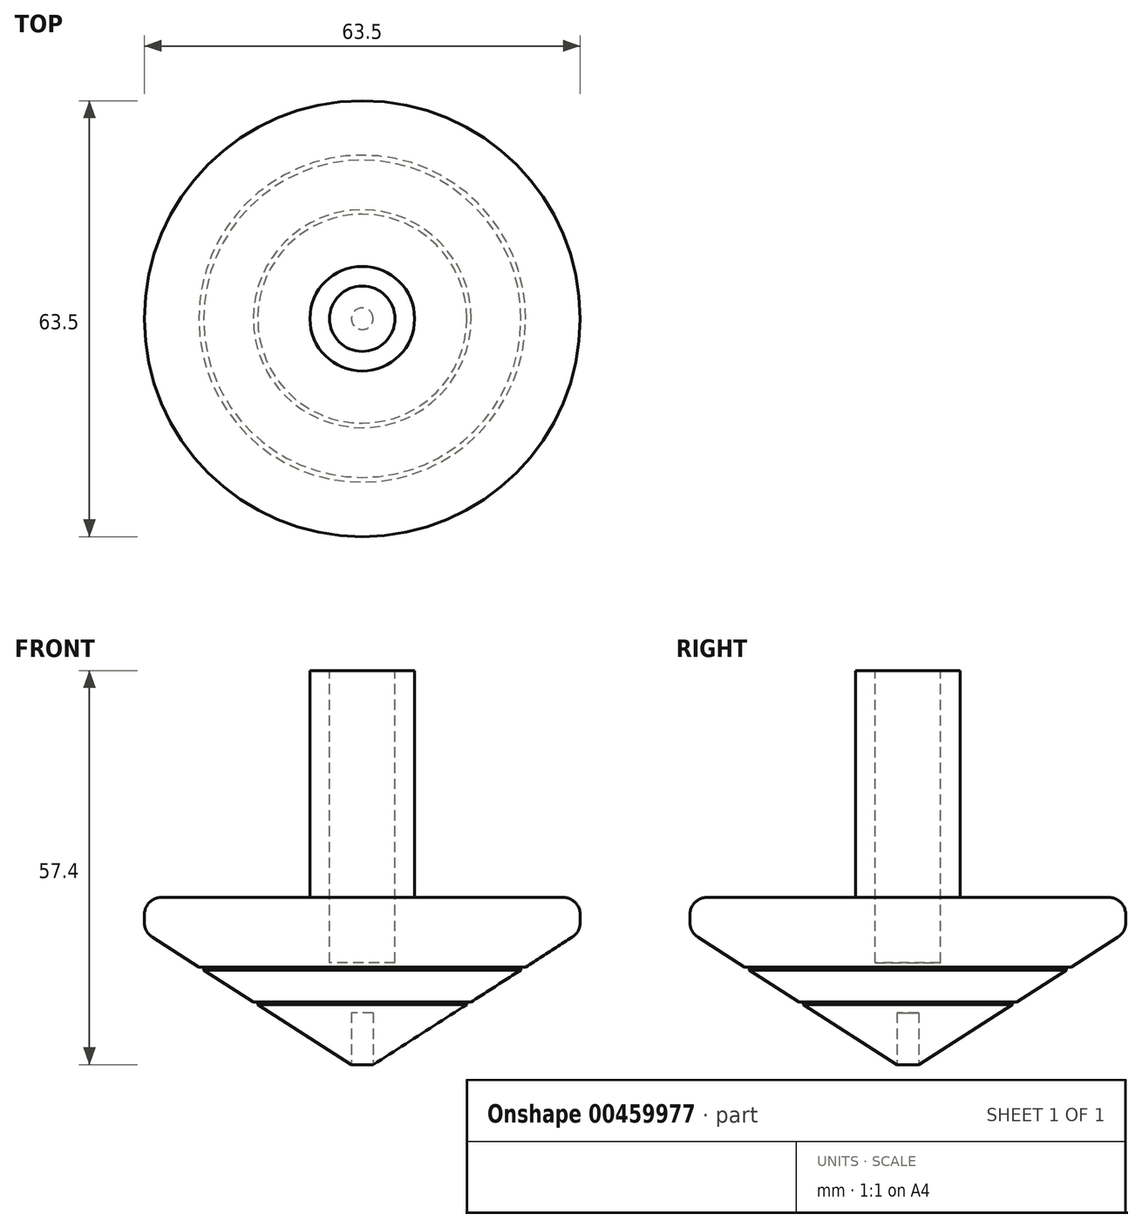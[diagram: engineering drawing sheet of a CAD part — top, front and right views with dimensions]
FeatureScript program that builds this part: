
annotation { "Feature Type Name" : "Feature", "Feature Type Description" : "" }
export const myFeature = defineFeature(function(context is Context, id is Id, definition is map)
    precondition{}
    {
        {
            var Q0;
            Q0=qCreatedBy(makeId("Front.planeOp"),FACE);
            var sketch = newSketch(context, id + "F0", { "sketchPlane" : qUnion([Q0])});
            skLineSegment(sketch, "E0", {"start": v(0, 0) * mm, "end": v(31.75, 20.32) * mm});
            skLineSegment(sketch, "E1", {"start": v(31.75, 20.32) * mm, "end": v(31.75, 25.4) * mm});
            skLineSegment(sketch, "E2", {"start": v(31.75, 25.4) * mm, "end": v(7.62, 25.4) * mm});
            skLineSegment(sketch, "E3", {"start": v(7.62, 25.4) * mm, "end": v(7.62, 58.42) * mm});
            skLineSegment(sketch, "E4", {"start": v(7.62, 58.42) * mm, "end": v(0, 58.42) * mm});
            skLineSegment(sketch, "E5", {"start": v(0, 58.42) * mm, "end": v(0, 0) * mm});
            skSolve(sketch);
        }
        {
            var Q0;
            Q0=makeQuery(id+"F0.imprint","IMPRINT",FACE,{"disambiguationData":[TD([[makeQuery(id+"F0.imprint","IMPRINT",EDGE,{"derivedFrom":sQuery(id+"F0.wireOp",EDGE,"E0")}),1.0]])]});
            var Q1;
            Q1=sQuery(id+"F0.wireOp",EDGE,"E5");
            revolve(context, id + "F1", {"entities" : qUnion([Q0]), "axis" : qUnion([Q1]), "revolveType" : RevolveType.FULL});
        }
        {
            var Q0;
            Q0=makeQuery(id+"F1.opRevolve","SWEPT_FACE",FACE,{"disambiguationData":[OSD([sQuery(id+"F0.wireOp",EDGE,"E1")])]});
            fillet(context, id + "F2", {"entities" : qUnion([Q0]), "radius" : 2.54 * mm, "tangentPropagation" : true, "allowEdgeOverflow" : false});
        }
        {
            var Q0;
            Q0=qCreatedBy(makeId("Top.planeOp"),FACE);
            var sketch = newSketch(context, id + "F3", { "sketchPlane" : qUnion([Q0])});
            skCircle(sketch, "E6", {"center": v(0, 0) * mm, "radius": 1.59 * mm});
            skSolve(sketch);
        }
        {
            var Q0;
            Q0=qSketchRegion(id+"F3",true);
            extrude(context, id + "F4", {"entities" : qUnion([Q0]), "operationType" : NewBodyOperationType.REMOVE, "depth" : 8.57 * mm});
        }
        {
            var Q0;
            Q0=makeQuery(id+"F1.opRevolve","SWEPT_FACE",FACE,{"disambiguationData":[OSD([sQuery(id+"F0.wireOp",EDGE,"E4")])]});
            var sketch = newSketch(context, id + "F5", { "sketchPlane" : qUnion([Q0])});
            skCircle(sketch, "E7", {"center": v(0, 0) * mm, "radius": 4.76 * mm});
            skSolve(sketch);
        }
        {
            var Q0;
            Q0=qSketchRegion(id+"F5",true);
            extrude(context, id + "F6", {"entities" : qUnion([Q0]), "operationType" : NewBodyOperationType.REMOVE, "oppositeDirection" : true, "depth" : 42.55 * mm});
        }
        {
            var Q0;
            Q0=qCreatedBy(makeId("Top.planeOp"),FACE);
            var sketch = newSketch(context, id + "F7", { "sketchPlane" : qUnion([Q0])});
            skCircle(sketch, "E8", {"center": v(0, 0) * mm, "radius": 17.57 * mm});
            skCircle(sketch, "E9", {"center": v(0, 0) * mm, "radius": 15.23 * mm});
            skSolve(sketch);
        }
        {
            var Q0;
            Q0 = qSketchRegion(id + "F7", true);
            extrude(context, id + "F8", {"entities" : qUnion([Q0]), "operationType" : NewBodyOperationType.REMOVE, "depth" : 10.16 * mm});
        }
        {
            var Q0;
            Q0=qCreatedBy(makeId("Top.planeOp"),FACE);
            var sketch = newSketch(context, id + "F9", { "sketchPlane" : qUnion([Q0])});
            skCircle(sketch, "E10", {"center": v(0, 0) * mm, "radius": 23.1 * mm});
            skCircle(sketch, "E11", {"center": v(0, 0) * mm, "radius": 24.25 * mm});
            skSolve(sketch);
        }
        {
            var Q0;
            Q0 = qSketchRegion(id + "F9", true);
            extrude(context, id + "F10", {"entities" : qUnion([Q0]), "operationType" : NewBodyOperationType.REMOVE, "depth" : 15.24 * mm});
        }
    });
